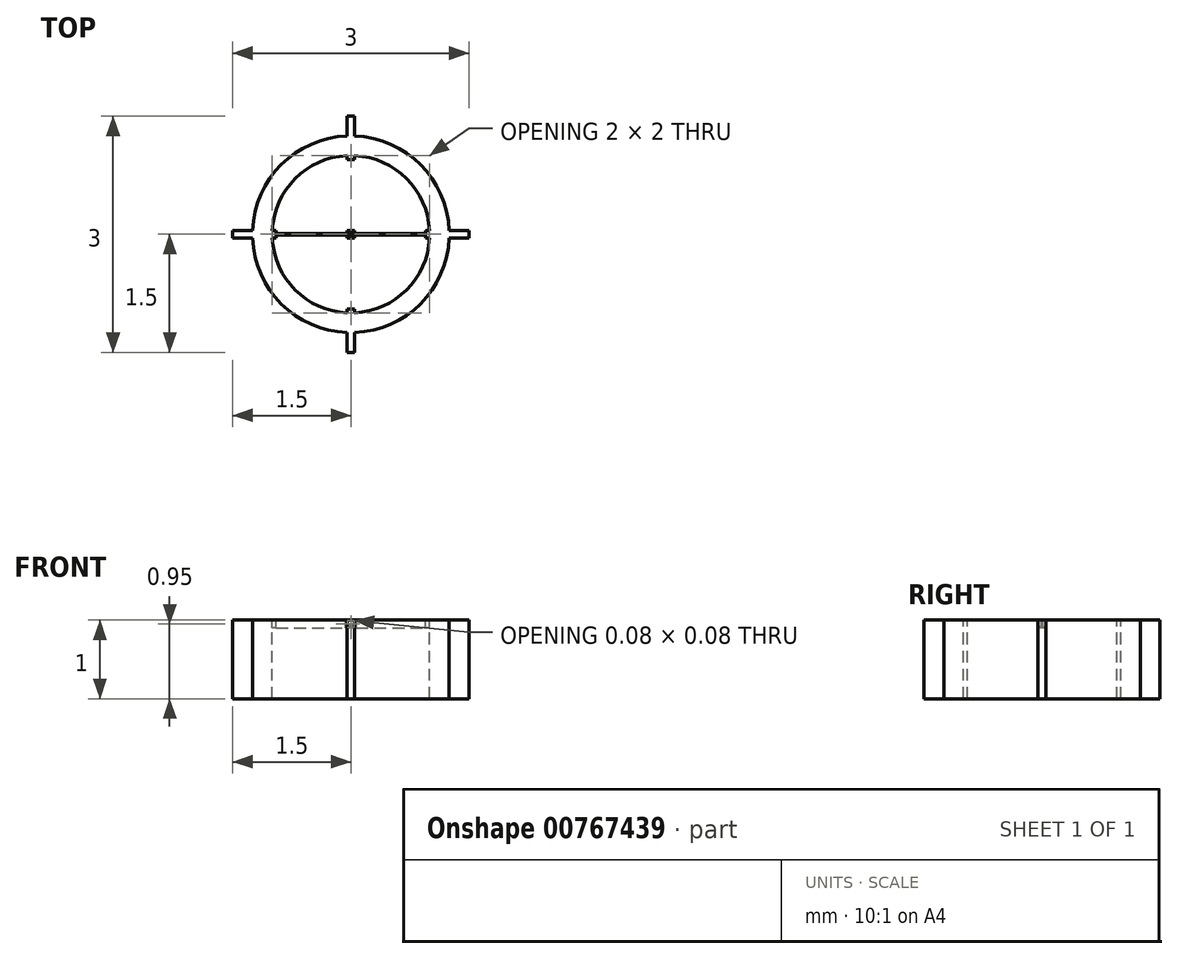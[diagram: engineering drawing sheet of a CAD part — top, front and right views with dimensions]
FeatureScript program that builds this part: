
annotation { "Feature Type Name" : "Feature", "Feature Type Description" : "" }
export const myFeature = defineFeature(function(context is Context, id is Id, definition is map)
    precondition{}
    {
        {
            var Q0;
            Q0=qCreatedBy(makeId("Top.planeOp"),FACE);
            var sketch = newSketch(context, id + "F0", { "sketchPlane" : qUnion([Q0])});
            skCircle(sketch, "E0", {"center": v(0, 0) * mm, "radius": 1 * mm});
            skCircle(sketch, "E1", {"center": v(0, 0) * mm, "radius": 1.25 * mm});
            skLineSegment(sketch, "E2.bottom", {"start": v(1.5, 0.05) * mm, "end": v(-1.5, 0.05) * mm});
            skLineSegment(sketch, "E2.top", {"start": v(1.5, -0.05) * mm, "end": v(-1.5, -0.05) * mm});
            skLineSegment(sketch, "E2.left", {"start": v(1.5, 0.05) * mm, "end": v(1.5, -0.05) * mm});
            skLineSegment(sketch, "E2.right", {"start": v(-1.5, 0.05) * mm, "end": v(-1.5, -0.05) * mm});
            skLineSegment(sketch, "E3.bottom", {"start": v(0.05, 1.5) * mm, "end": v(-0.05, 1.5) * mm});
            skLineSegment(sketch, "E3.top", {"start": v(0.05, -1.5) * mm, "end": v(-0.05, -1.5) * mm});
            skLineSegment(sketch, "E3.left", {"start": v(0.05, 1.5) * mm, "end": v(0.05, -1.5) * mm});
            skLineSegment(sketch, "E3.right", {"start": v(-0.05, 1.5) * mm, "end": v(-0.05, -1.5) * mm});
            skCircle(sketch, "E4", {"center": v(0, 0) * mm, "radius": 0.04 * mm});
            skLineSegment(sketch, "E5.bottom", {"start": v(-0.95, 0.05) * mm, "end": v(-0.07, 0.05) * mm});
            skLineSegment(sketch, "E5.top", {"start": v(-0.95, -0.05) * mm, "end": v(-0.07, -0.05) * mm});
            skLineSegment(sketch, "E5.left", {"start": v(-0.95, 0.05) * mm, "end": v(-0.95, -0.05) * mm});
            skLineSegment(sketch, "E5.right", {"start": v(-0.07, 0.05) * mm, "end": v(-0.07, -0.05) * mm});
            skLineSegment(sketch, "E6.bottom", {"start": v(-0.95, 0) * mm, "end": v(-0.07, 0) * mm});
            skLineSegment(sketch, "E6.top", {"start": v(-0.95, -0.01) * mm, "end": v(-0.07, -0.01) * mm});
            skLineSegment(sketch, "E6.left", {"start": v(-0.95, 0) * mm, "end": v(-0.95, -0.01) * mm});
            skLineSegment(sketch, "E6.right", {"start": v(-0.07, 0) * mm, "end": v(-0.07, -0.01) * mm});
            skLineSegment(sketch, "E7.bottom", {"start": v(0.07, 0.05) * mm, "end": v(0.95, 0.05) * mm});
            skLineSegment(sketch, "E7.top", {"start": v(0.07, -0.05) * mm, "end": v(0.95, -0.05) * mm});
            skLineSegment(sketch, "E7.left", {"start": v(0.07, 0.05) * mm, "end": v(0.07, -0.05) * mm});
            skLineSegment(sketch, "E7.right", {"start": v(0.95, 0.05) * mm, "end": v(0.95, -0.05) * mm});
            skLineSegment(sketch, "E8.bottom", {"start": v(0.07, 0) * mm, "end": v(0.95, 0) * mm});
            skLineSegment(sketch, "E8.top", {"start": v(0.07, -0.01) * mm, "end": v(0.95, -0.01) * mm});
            skLineSegment(sketch, "E8.left", {"start": v(0.07, 0) * mm, "end": v(0.07, -0.01) * mm});
            skLineSegment(sketch, "E8.right", {"start": v(0.95, 0) * mm, "end": v(0.95, -0.01) * mm});
            skLineSegment(sketch, "E9.bottom", {"start": v(-0.05, 0.95) * mm, "end": v(0.05, 0.95) * mm});
            skLineSegment(sketch, "E9.top", {"start": v(-0.05, 0.17) * mm, "end": v(0.05, 0.17) * mm});
            skLineSegment(sketch, "E9.left", {"start": v(-0.05, 0.95) * mm, "end": v(-0.05, 0.17) * mm});
            skLineSegment(sketch, "E9.right", {"start": v(0.05, 0.95) * mm, "end": v(0.05, 0.17) * mm});
            skLineSegment(sketch, "E10.bottom", {"start": v(0, 0.95) * mm, "end": v(0.01, 0.95) * mm});
            skLineSegment(sketch, "E10.top", {"start": v(0, 0.17) * mm, "end": v(0.01, 0.17) * mm});
            skLineSegment(sketch, "E10.left", {"start": v(0, 0.95) * mm, "end": v(0, 0.17) * mm});
            skLineSegment(sketch, "E10.right", {"start": v(0.01, 0.95) * mm, "end": v(0.01, 0.17) * mm});
            skLineSegment(sketch, "E11.bottom", {"start": v(-0.05, -0.95) * mm, "end": v(0.05, -0.95) * mm});
            skLineSegment(sketch, "E11.top", {"start": v(-0.05, -0.17) * mm, "end": v(0.05, -0.17) * mm});
            skLineSegment(sketch, "E11.left", {"start": v(-0.05, -0.95) * mm, "end": v(-0.05, -0.17) * mm});
            skLineSegment(sketch, "E11.right", {"start": v(0.05, -0.95) * mm, "end": v(0.05, -0.17) * mm});
            skLineSegment(sketch, "E12.bottom", {"start": v(0, -0.17) * mm, "end": v(0.01, -0.17) * mm});
            skLineSegment(sketch, "E12.top", {"start": v(0, -0.95) * mm, "end": v(0.01, -0.95) * mm});
            skLineSegment(sketch, "E12.left", {"start": v(0, -0.17) * mm, "end": v(0, -0.95) * mm});
            skLineSegment(sketch, "E12.right", {"start": v(0.01, -0.17) * mm, "end": v(0.01, -0.95) * mm});
            skCircle(sketch, "E13", {"center": v(0, 0) * mm, "radius": 0.9 * mm});
            skSolve(sketch);
        }
        {
            var Q0;
            Q0=makeQuery(id+"F0.imprint","IMPRINT",FACE,{"disambiguationData":[TD([[makeQuery(id+"F0.imprint","IMPRINT",EDGE,{"derivedFrom":sQuery(id+"F0.wireOp",EDGE,"E0")}),-1.0]])]});
            var Q1;
            {var subQ3=sQuery(id+"F0.wireOp",EDGE,"E6.left");Q1=makeQuery(id+"F0.imprint","IMPRINT",FACE,{"disambiguationData":[TD([[makeQuery(id+"F0.imprint","IMPRINT",EDGE,{"derivedFrom":subQ3}),-1.0]])]});}
            var Q2;
            {var subQ0=sQuery(id+"F0.wireOp",EDGE,"E3.left");var subQ1=sQuery(id+"F0.wireOp",EDGE,"E0");var subQ2=makeQuery(id+"F0.imprint","INTERSECT",VERTEX,{"disambiguationData":[OD(0.0)],"derivedFrom":[subQ1,subQ0]});Q2=makeQuery(id+"F0.imprint","IMPRINT",FACE,{"disambiguationData":[TD([[makeQuery(id+"F0.imprint","IMPRINT",EDGE,{"disambiguationData":[TD([[subQ2,-1.0]])],"derivedFrom":subQ1}),1.0]])]});}
            var Q3;
            {var subQ0=sQuery(id+"F0.wireOp",EDGE,"E3.right");var subQ1=sQuery(id+"F0.wireOp",EDGE,"E0");var subQ2=makeQuery(id+"F0.imprint","INTERSECT",VERTEX,{"disambiguationData":[OD(1.0)],"derivedFrom":[subQ1,subQ0]});Q3=makeQuery(id+"F0.imprint","IMPRINT",FACE,{"disambiguationData":[TD([[makeQuery(id+"F0.imprint","IMPRINT",EDGE,{"disambiguationData":[TD([[subQ2,-1.0]])],"derivedFrom":subQ1}),1.0]])]});}
            var Q4;
            {var subQ7=sQuery(id+"F0.wireOp",EDGE,"E8.right");Q4=makeQuery(id+"F0.imprint","IMPRINT",FACE,{"disambiguationData":[TD([[makeQuery(id+"F0.imprint","IMPRINT",EDGE,{"derivedFrom":subQ7}),1.0]])]});}
            var Q5;
            {var subQ5=sQuery(id+"F0.wireOp",EDGE,"E2.right");Q5=makeQuery(id+"F0.imprint","IMPRINT",FACE,{"disambiguationData":[TD([[makeQuery(id+"F0.imprint","IMPRINT",EDGE,{"derivedFrom":subQ5}),1.0]])]});}
            var Q6;
            {var subQ5=sQuery(id+"F0.wireOp",EDGE,"E3.bottom");Q6=makeQuery(id+"F0.imprint","IMPRINT",FACE,{"disambiguationData":[TD([[makeQuery(id+"F0.imprint","IMPRINT",EDGE,{"derivedFrom":subQ5}),1.0]])]});}
            var Q7;
            {var subQ5=sQuery(id+"F0.wireOp",EDGE,"E2.left");Q7=makeQuery(id+"F0.imprint","IMPRINT",FACE,{"disambiguationData":[TD([[makeQuery(id+"F0.imprint","IMPRINT",EDGE,{"derivedFrom":subQ5}),-1.0]])]});}
            var Q8;
            {var subQ5=sQuery(id+"F0.wireOp",EDGE,"E3.top");Q8=makeQuery(id+"F0.imprint","IMPRINT",FACE,{"disambiguationData":[TD([[makeQuery(id+"F0.imprint","IMPRINT",EDGE,{"derivedFrom":subQ5}),-1.0]])]});}
            extrude(context, id + "F1", {"entities" : qUnion([Q0, Q1, Q2, Q3, Q4, Q5, Q6, Q7, Q8]), "oppositeDirection" : true, "depth" : 1 * mm, "offsetDistance" : 25 * mm});
        }
        {
            var Q0;
            {var subQ5=sQuery(id+"F0.wireOp",EDGE,"E2.right");Q0=makeQuery(id+"F0.imprint","IMPRINT",FACE,{"disambiguationData":[TD([[makeQuery(id+"F0.imprint","IMPRINT",EDGE,{"derivedFrom":subQ5}),1.0]])]});}
            var Q1;
            {var subQ0=sQuery(id+"F0.wireOp",EDGE,"E2.bottom");var subQ1=sQuery(id+"F0.wireOp",EDGE,"E0");var subQ2=makeQuery(id+"F0.imprint","INTERSECT",VERTEX,{"disambiguationData":[OD(1.0)],"derivedFrom":[subQ1,subQ0]});Q1=makeQuery(id+"F0.imprint","IMPRINT",FACE,{"disambiguationData":[TD([[makeQuery(id+"F0.imprint","IMPRINT",EDGE,{"disambiguationData":[TD([[subQ2,-1.0]])],"derivedFrom":subQ1}),-1.0]])]});}
            var Q2;
            {var subQ0=sQuery(id+"F0.wireOp",EDGE,"E2.bottom");var subQ1=sQuery(id+"F0.wireOp",EDGE,"E0");var subQ2=makeQuery(id+"F0.imprint","INTERSECT",VERTEX,{"disambiguationData":[OD(1.0)],"derivedFrom":[subQ1,subQ0]});Q2=makeQuery(id+"F0.imprint","IMPRINT",FACE,{"disambiguationData":[TD([[makeQuery(id+"F0.imprint","IMPRINT",EDGE,{"disambiguationData":[TD([[subQ2,-1.0]])],"derivedFrom":subQ1}),1.0]])]});}
            var Q3;
            {var subQ0=sQuery(id+"F0.wireOp",EDGE,"E2.bottom");var subQ1=sQuery(id+"F0.wireOp",EDGE,"E0");var subQ2=makeQuery(id+"F0.imprint","INTERSECT",VERTEX,{"disambiguationData":[OD(0.0)],"derivedFrom":[subQ1,subQ0]});Q3=makeQuery(id+"F0.imprint","IMPRINT",FACE,{"disambiguationData":[TD([[makeQuery(id+"F0.imprint","IMPRINT",EDGE,{"disambiguationData":[TD([[subQ2,1.0]])],"derivedFrom":subQ1}),1.0]])]});}
            var Q4;
            {var subQ0=sQuery(id+"F0.wireOp",EDGE,"E2.bottom");var subQ1=sQuery(id+"F0.wireOp",EDGE,"E0");var subQ2=makeQuery(id+"F0.imprint","INTERSECT",VERTEX,{"disambiguationData":[OD(0.0)],"derivedFrom":[subQ1,subQ0]});Q4=makeQuery(id+"F0.imprint","IMPRINT",FACE,{"disambiguationData":[TD([[makeQuery(id+"F0.imprint","IMPRINT",EDGE,{"disambiguationData":[TD([[subQ2,1.0]])],"derivedFrom":subQ1}),-1.0]])]});}
            var Q5;
            {var subQ5=sQuery(id+"F0.wireOp",EDGE,"E2.left");Q5=makeQuery(id+"F0.imprint","IMPRINT",FACE,{"disambiguationData":[TD([[makeQuery(id+"F0.imprint","IMPRINT",EDGE,{"derivedFrom":subQ5}),-1.0]])]});}
            var Q6;
            {var subQ0=sQuery(id+"F0.wireOp",EDGE,"E3.left");var subQ1=sQuery(id+"F0.wireOp",EDGE,"E0");var subQ2=makeQuery(id+"F0.imprint","INTERSECT",VERTEX,{"disambiguationData":[OD(0.0)],"derivedFrom":[subQ1,subQ0]});Q6=makeQuery(id+"F0.imprint","IMPRINT",FACE,{"disambiguationData":[TD([[makeQuery(id+"F0.imprint","IMPRINT",EDGE,{"disambiguationData":[TD([[subQ2,-1.0]])],"derivedFrom":subQ1}),1.0]])]});}
            var Q7;
            {var subQ0=sQuery(id+"F0.wireOp",EDGE,"E3.left");var subQ1=sQuery(id+"F0.wireOp",EDGE,"E0");var subQ2=makeQuery(id+"F0.imprint","INTERSECT",VERTEX,{"disambiguationData":[OD(0.0)],"derivedFrom":[subQ1,subQ0]});Q7=makeQuery(id+"F0.imprint","IMPRINT",FACE,{"disambiguationData":[TD([[makeQuery(id+"F0.imprint","IMPRINT",EDGE,{"disambiguationData":[TD([[subQ2,-1.0]])],"derivedFrom":subQ1}),-1.0]])]});}
            var Q8;
            {var subQ5=sQuery(id+"F0.wireOp",EDGE,"E3.bottom");Q8=makeQuery(id+"F0.imprint","IMPRINT",FACE,{"disambiguationData":[TD([[makeQuery(id+"F0.imprint","IMPRINT",EDGE,{"derivedFrom":subQ5}),1.0]])]});}
            var Q9;
            {var subQ0=sQuery(id+"F0.wireOp",EDGE,"E3.right");var subQ1=sQuery(id+"F0.wireOp",EDGE,"E0");var subQ2=makeQuery(id+"F0.imprint","INTERSECT",VERTEX,{"disambiguationData":[OD(1.0)],"derivedFrom":[subQ1,subQ0]});Q9=makeQuery(id+"F0.imprint","IMPRINT",FACE,{"disambiguationData":[TD([[makeQuery(id+"F0.imprint","IMPRINT",EDGE,{"disambiguationData":[TD([[subQ2,-1.0]])],"derivedFrom":subQ1}),1.0]])]});}
            var Q10;
            {var subQ0=sQuery(id+"F0.wireOp",EDGE,"E3.right");var subQ1=sQuery(id+"F0.wireOp",EDGE,"E0");var subQ2=makeQuery(id+"F0.imprint","INTERSECT",VERTEX,{"disambiguationData":[OD(1.0)],"derivedFrom":[subQ1,subQ0]});Q10=makeQuery(id+"F0.imprint","IMPRINT",FACE,{"disambiguationData":[TD([[makeQuery(id+"F0.imprint","IMPRINT",EDGE,{"disambiguationData":[TD([[subQ2,-1.0]])],"derivedFrom":subQ1}),-1.0]])]});}
            var Q11;
            {var subQ5=sQuery(id+"F0.wireOp",EDGE,"E3.top");Q11=makeQuery(id+"F0.imprint","IMPRINT",FACE,{"disambiguationData":[TD([[makeQuery(id+"F0.imprint","IMPRINT",EDGE,{"derivedFrom":subQ5}),-1.0]])]});}
            var Q12;
            Q12=makeQuery(id+"F0.imprint","IMPRINT",FACE,{"disambiguationData":[TD([[makeQuery(id+"F0.imprint","IMPRINT",EDGE,{"derivedFrom":sQuery(id+"F0.wireOp",EDGE,"E4")}),1.0]])]});
            var Q13;
            Q13=makeQuery(id+"F0.imprint","IMPRINT",FACE,{"disambiguationData":[TD([[makeQuery(id+"F0.imprint","IMPRINT",EDGE,{"derivedFrom":sQuery(id+"F0.wireOp",EDGE,"E4")}),-1.0]])]});
            var Q14;
            Q14=makeQuery(id+"F0.imprint","IMPRINT",FACE,{"disambiguationData":[TD([[makeQuery(id+"F0.imprint","IMPRINT",EDGE,{"derivedFrom":sQuery(id+"F0.wireOp",EDGE,"E6.bottom")}),-1.0]])]});
            var Q15;
            {var subQ7=sQuery(id+"F0.wireOp",EDGE,"E6.right");Q15=makeQuery(id+"F0.imprint","IMPRINT",FACE,{"disambiguationData":[TD([[makeQuery(id+"F0.imprint","IMPRINT",EDGE,{"derivedFrom":subQ7}),1.0]])]});}
            var Q16;
            {var subQ5=sQuery(id+"F0.wireOp",EDGE,"E8.left");Q16=makeQuery(id+"F0.imprint","IMPRINT",FACE,{"disambiguationData":[TD([[makeQuery(id+"F0.imprint","IMPRINT",EDGE,{"derivedFrom":subQ5}),-1.0]])]});}
            var Q17;
            {var subQ8=sQuery(id+"F0.wireOp",EDGE,"E12.bottom");Q17=makeQuery(id+"F0.imprint","IMPRINT",FACE,{"disambiguationData":[TD([[makeQuery(id+"F0.imprint","IMPRINT",EDGE,{"derivedFrom":subQ8}),1.0]])]});}
            var Q18;
            Q18=makeQuery(id+"F0.imprint","IMPRINT",FACE,{"disambiguationData":[TD([[makeQuery(id+"F0.imprint","IMPRINT",EDGE,{"derivedFrom":sQuery(id+"F0.wireOp",EDGE,"E10.bottom")}),-1.0]])]});
            var Q19;
            Q19=makeQuery(id+"F0.imprint","IMPRINT",FACE,{"disambiguationData":[TD([[makeQuery(id+"F0.imprint","IMPRINT",EDGE,{"derivedFrom":sQuery(id+"F0.wireOp",EDGE,"E12.bottom")}),-1.0]])]});
            var Q20;
            Q20=makeQuery(id+"F0.imprint","IMPRINT",FACE,{"disambiguationData":[TD([[makeQuery(id+"F0.imprint","IMPRINT",EDGE,{"derivedFrom":sQuery(id+"F0.wireOp",EDGE,"E8.bottom")}),-1.0]])]});
            var Q21;
            {var subQ3=sQuery(id+"F0.wireOp",EDGE,"E10.top");Q21=makeQuery(id+"F0.imprint","IMPRINT",FACE,{"disambiguationData":[TD([[makeQuery(id+"F0.imprint","IMPRINT",EDGE,{"derivedFrom":subQ3}),-1.0]])]});}
            var Q22;
            {var subQ0=sQuery(id+"F0.wireOp",EDGE,"E10.top");Q22=makeQuery(id+"F0.imprint","IMPRINT",FACE,{"disambiguationData":[TD([[makeQuery(id+"F0.imprint","IMPRINT",EDGE,{"derivedFrom":subQ0}),1.0]])]});}
            var Q23;
            {var subQ0=sQuery(id+"F0.wireOp",EDGE,"E12.top");Q23=makeQuery(id+"F0.imprint","IMPRINT",FACE,{"disambiguationData":[TD([[makeQuery(id+"F0.imprint","IMPRINT",EDGE,{"derivedFrom":subQ0}),1.0]])]});}
            extrude(context, id + "F2", {"entities" : qUnion([Q0, Q1, Q2, Q3, Q4, Q5, Q6, Q7, Q8, Q9, Q10, Q11, Q12, Q13, Q14, Q15, Q16, Q17, Q18, Q19, Q20, Q21, Q22, Q23]), "operationType" : NewBodyOperationType.ADD, "oppositeDirection" : true, "depth" : 0.1 * mm, "offsetDistance" : 25 * mm});
        }
        {
            var Q0;
            Q0=makeQuery(id+"F0.imprint","IMPRINT",FACE,{"disambiguationData":[TD([[makeQuery(id+"F0.imprint","IMPRINT",EDGE,{"derivedFrom":sQuery(id+"F0.wireOp",EDGE,"E4")}),1.0]])]});
            var Q1;
            Q1=sQuery(id+"F0.wireOp",EDGE,"E4");
            var Q2;
            Q2=sQuery(id+"F0.wireOp",EDGE,"E2.bottom");
            revolve(context, id + "F3", {"operationType" : NewBodyOperationType.REMOVE, "surfaceOperationType" : NewSurfaceOperationType.NEW, "entities" : qUnion([Q0]), "surfaceEntities" : qUnion([Q1]), "axis" : qUnion([Q2]), "revolveType" : RevolveType.ONE_DIRECTION, "oppositeDirection" : true, "angle" : 180 * degree});
        }
        {
            var Q0;
            Q0=makeQuery(id+"F0.imprint","IMPRINT",FACE,{"disambiguationData":[TD([[makeQuery(id+"F0.imprint","IMPRINT",EDGE,{"derivedFrom":sQuery(id+"F0.wireOp",EDGE,"E4")}),1.0]])]});
            var Q1;
            Q1=sQuery(id+"F0.wireOp",EDGE,"E4");
            var Q2;
            Q2=sQuery(id+"F0.wireOp",EDGE,"E2.top");
            revolve(context, id + "F4", {"operationType" : NewBodyOperationType.REMOVE, "surfaceOperationType" : NewSurfaceOperationType.NEW, "entities" : qUnion([Q0]), "surfaceEntities" : qUnion([Q1]), "axis" : qUnion([Q2]), "revolveType" : RevolveType.ONE_DIRECTION, "angle" : 180 * degree});
        }
        {
            var Q0;
            {var subQ3=sQuery(id+"F0.wireOp",EDGE,"E13");var subQ5=sQuery(id+"F0.wireOp",EDGE,"E7.bottom");var subQ6=makeQuery(id+"F0.imprint","INTERSECT",VERTEX,{"derivedFrom":[subQ5,subQ3]});Q0=makeQuery(id+"F0.imprint","IMPRINT",FACE,{"disambiguationData":[TD([[makeQuery(id+"F0.imprint","IMPRINT",EDGE,{"disambiguationData":[TD([[subQ6,-1.0]])],"derivedFrom":subQ3}),1.0]])]});}
            var Q1;
            {var subQ0=sQuery(id+"F0.wireOp",EDGE,"E9.left");var subQ5=sQuery(id+"F0.wireOp",EDGE,"E13");var subQ6=makeQuery(id+"F0.imprint","INTERSECT",VERTEX,{"derivedFrom":[subQ0,subQ5]});Q1=makeQuery(id+"F0.imprint","IMPRINT",FACE,{"disambiguationData":[TD([[makeQuery(id+"F0.imprint","IMPRINT",EDGE,{"disambiguationData":[TD([[subQ6,1.0]])],"derivedFrom":subQ5}),1.0]])]});}
            var Q2;
            {var subQ0=sQuery(id+"F0.wireOp",EDGE,"E9.right");var subQ5=sQuery(id+"F0.wireOp",EDGE,"E13");var subQ7=makeQuery(id+"F0.imprint","INTERSECT",VERTEX,{"derivedFrom":[subQ0,subQ5]});Q2=makeQuery(id+"F0.imprint","IMPRINT",FACE,{"disambiguationData":[TD([[makeQuery(id+"F0.imprint","IMPRINT",EDGE,{"disambiguationData":[TD([[subQ7,-1.0]])],"derivedFrom":subQ5}),1.0]])]});}
            var Q3;
            {var subQ0=sQuery(id+"F0.wireOp",EDGE,"E10.top");Q3=makeQuery(id+"F0.imprint","IMPRINT",FACE,{"disambiguationData":[TD([[makeQuery(id+"F0.imprint","IMPRINT",EDGE,{"derivedFrom":subQ0}),1.0]])]});}
            var Q4;
            {var subQ0=sQuery(id+"F0.wireOp",EDGE,"E11.left");var subQ5=sQuery(id+"F0.wireOp",EDGE,"E13");var subQ6=makeQuery(id+"F0.imprint","INTERSECT",VERTEX,{"derivedFrom":[subQ0,subQ5]});Q4=makeQuery(id+"F0.imprint","IMPRINT",FACE,{"disambiguationData":[TD([[makeQuery(id+"F0.imprint","IMPRINT",EDGE,{"disambiguationData":[TD([[subQ6,-1.0]])],"derivedFrom":subQ5}),1.0]])]});}
            var Q5;
            {var subQ3=sQuery(id+"F0.wireOp",EDGE,"E13");var subQ5=sQuery(id+"F0.wireOp",EDGE,"E5.top");var subQ8=makeQuery(id+"F0.imprint","INTERSECT",VERTEX,{"derivedFrom":[subQ5,subQ3]});Q5=makeQuery(id+"F0.imprint","IMPRINT",FACE,{"disambiguationData":[TD([[makeQuery(id+"F0.imprint","IMPRINT",EDGE,{"disambiguationData":[TD([[subQ8,-1.0]])],"derivedFrom":subQ3}),1.0]])]});}
            var Q6;
            {var subQ1=sQuery(id+"F0.wireOp",EDGE,"E5.top");var subQ3=sQuery(id+"F0.wireOp",EDGE,"E13");var subQ4=makeQuery(id+"F0.imprint","INTERSECT",VERTEX,{"derivedFrom":[subQ1,subQ3]});Q6=makeQuery(id+"F0.imprint","IMPRINT",FACE,{"disambiguationData":[TD([[makeQuery(id+"F0.imprint","IMPRINT",EDGE,{"disambiguationData":[TD([[subQ4,1.0]])],"derivedFrom":subQ3}),1.0]])]});}
            var Q7;
            {var subQ0=sQuery(id+"F0.wireOp",EDGE,"E5.bottom");var subQ3=sQuery(id+"F0.wireOp",EDGE,"E13");var subQ4=makeQuery(id+"F0.imprint","INTERSECT",VERTEX,{"derivedFrom":[subQ0,subQ3]});Q7=makeQuery(id+"F0.imprint","IMPRINT",FACE,{"disambiguationData":[TD([[makeQuery(id+"F0.imprint","IMPRINT",EDGE,{"disambiguationData":[TD([[subQ4,1.0]])],"derivedFrom":subQ3}),1.0]])]});}
            var Q8;
            {var subQ0=sQuery(id+"F0.wireOp",EDGE,"E6.right");Q8=makeQuery(id+"F0.imprint","IMPRINT",FACE,{"disambiguationData":[TD([[makeQuery(id+"F0.imprint","IMPRINT",EDGE,{"derivedFrom":subQ0}),-1.0]])]});}
            var Q9;
            {var subQ1=sQuery(id+"F0.wireOp",EDGE,"E5.bottom");var subQ3=sQuery(id+"F0.wireOp",EDGE,"E13");var subQ4=makeQuery(id+"F0.imprint","INTERSECT",VERTEX,{"derivedFrom":[subQ1,subQ3]});Q9=makeQuery(id+"F0.imprint","IMPRINT",FACE,{"disambiguationData":[TD([[makeQuery(id+"F0.imprint","IMPRINT",EDGE,{"disambiguationData":[TD([[subQ4,-1.0]])],"derivedFrom":subQ3}),1.0]])]});}
            var Q10;
            {var subQ0=sQuery(id+"F0.wireOp",EDGE,"E8.left");Q10=makeQuery(id+"F0.imprint","IMPRINT",FACE,{"disambiguationData":[TD([[makeQuery(id+"F0.imprint","IMPRINT",EDGE,{"derivedFrom":subQ0}),1.0]])]});}
            var Q11;
            {var subQ1=sQuery(id+"F0.wireOp",EDGE,"E7.bottom");var subQ3=sQuery(id+"F0.wireOp",EDGE,"E13");var subQ4=makeQuery(id+"F0.imprint","INTERSECT",VERTEX,{"derivedFrom":[subQ1,subQ3]});Q11=makeQuery(id+"F0.imprint","IMPRINT",FACE,{"disambiguationData":[TD([[makeQuery(id+"F0.imprint","IMPRINT",EDGE,{"disambiguationData":[TD([[subQ4,1.0]])],"derivedFrom":subQ3}),1.0]])]});}
            var Q12;
            {var subQ1=sQuery(id+"F0.wireOp",EDGE,"E7.top");var subQ3=sQuery(id+"F0.wireOp",EDGE,"E13");var subQ4=makeQuery(id+"F0.imprint","INTERSECT",VERTEX,{"derivedFrom":[subQ1,subQ3]});Q12=makeQuery(id+"F0.imprint","IMPRINT",FACE,{"disambiguationData":[TD([[makeQuery(id+"F0.imprint","IMPRINT",EDGE,{"disambiguationData":[TD([[subQ4,-1.0]])],"derivedFrom":subQ3}),1.0]])]});}
            var Q13;
            {var subQ0=sQuery(id+"F0.wireOp",EDGE,"E11.right");var subQ5=sQuery(id+"F0.wireOp",EDGE,"E13");var subQ6=makeQuery(id+"F0.imprint","INTERSECT",VERTEX,{"derivedFrom":[subQ0,subQ5]});Q13=makeQuery(id+"F0.imprint","IMPRINT",FACE,{"disambiguationData":[TD([[makeQuery(id+"F0.imprint","IMPRINT",EDGE,{"disambiguationData":[TD([[subQ6,1.0]])],"derivedFrom":subQ5}),1.0]])]});}
            var Q14;
            {var subQ0=sQuery(id+"F0.wireOp",EDGE,"E12.bottom");Q14=makeQuery(id+"F0.imprint","IMPRINT",FACE,{"disambiguationData":[TD([[makeQuery(id+"F0.imprint","IMPRINT",EDGE,{"derivedFrom":subQ0}),-1.0]])]});}
            extrude(context, id + "F5", {"entities" : qUnion([Q0, Q1, Q2, Q3, Q4, Q5, Q6, Q7, Q8, Q9, Q10, Q11, Q12, Q13, Q14]), "operationType" : NewBodyOperationType.REMOVE, "oppositeDirection" : true, "depth" : 1 * mm, "offsetDistance" : 25 * mm, "hasSecondDirection" : true, "secondDirectionOppositeDirection" : false, "secondDirectionDepth" : -.2 * mm});
        }
    });
